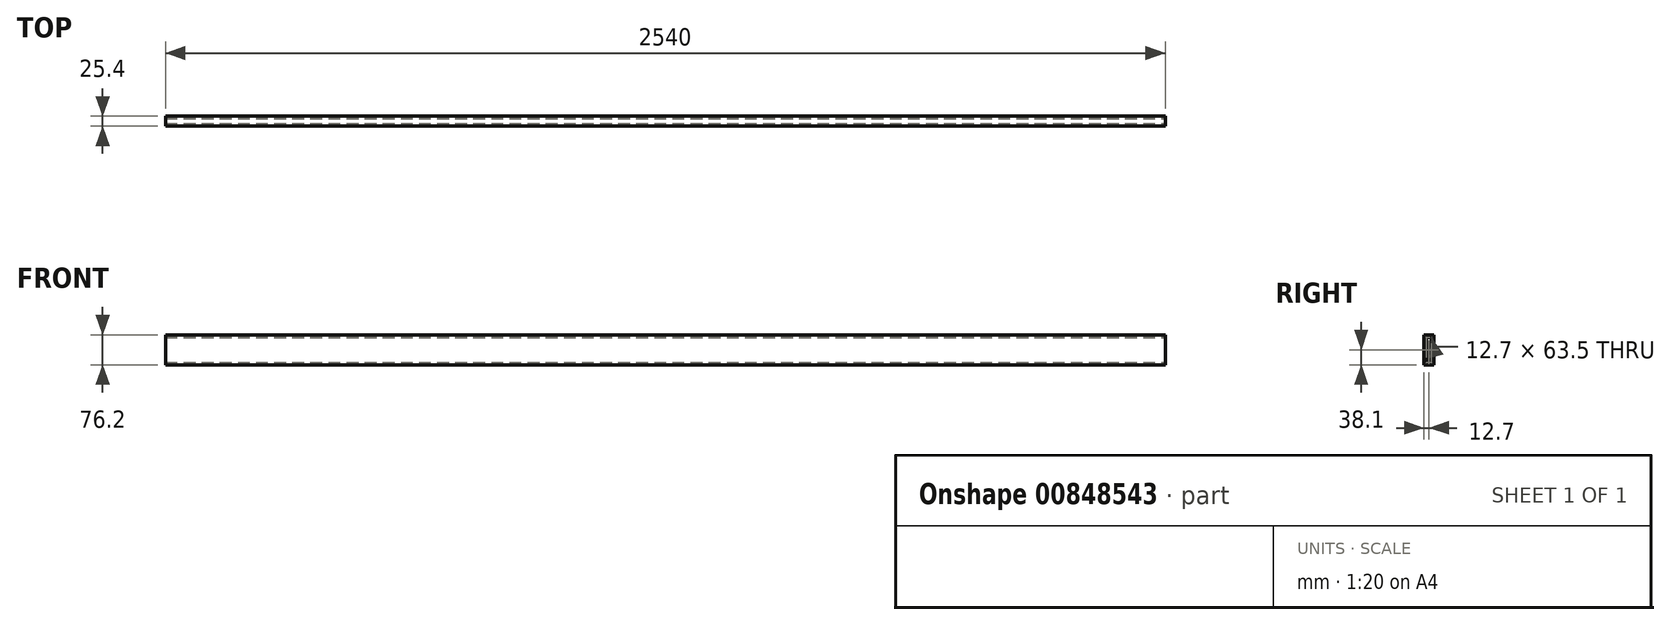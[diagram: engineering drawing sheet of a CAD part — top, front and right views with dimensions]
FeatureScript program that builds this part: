
annotation { "Feature Type Name" : "Feature", "Feature Type Description" : "" }
export const myFeature = defineFeature(function(context is Context, id is Id, definition is map)
    precondition{}
    {
        {
            var Q0;
            Q0=qCreatedBy(makeId("Top.planeOp"),FACE);
            var sketch = newSketch(context, id + "F0", { "sketchPlane" : qUnion([Q0])});
            skLineSegment(sketch, "E0.bottom", {"start": v(-1270, -12.7) * mm, "end": v(1270, -12.7) * mm});
            skLineSegment(sketch, "E0.top", {"start": v(-1270, 12.7) * mm, "end": v(1270, 12.7) * mm});
            skLineSegment(sketch, "E0.left", {"start": v(-1270, -12.7) * mm, "end": v(-1270, 12.7) * mm});
            skLineSegment(sketch, "E0.right", {"start": v(1270, -12.7) * mm, "end": v(1270, 12.7) * mm});
            skPoint(sketch, "E0.middle", {"position": v(0, 0) * mm});
            skSolve(sketch);
        }
        {
            var Q0;
            Q0 = qSketchRegion(id + "F0", true);
            extrude(context, id + "F1", {"entities" : qUnion([Q0]), "depth" : 76.2 * mm, "offsetDistance" : 25.4 * mm});
        }
        {
            var Q0;
            Q0=makeQuery(id+"F1.opExtrude","SWEPT_FACE",FACE,{"disambiguationData":[OSD([sQuery(id+"F0.wireOp",EDGE,"E0.right")])]});
            var Q1;
            Q1=makeQuery(id+"F1.opExtrude","SWEPT_FACE",FACE,{"disambiguationData":[OSD([sQuery(id+"F0.wireOp",EDGE,"E0.left")])]});
            var Q2;
            Q2=makeQuery(id+"F1.opExtrude","SWEPT_BODY",BODY,{"disambiguationData":[OSD([sQuery(id+"F0.wireOp",EDGE,"E0.bottom"),sQuery(id+"F0.wireOp",EDGE,"E0.top"),sQuery(id+"F0.wireOp",EDGE,"E0.left"),sQuery(id+"F0.wireOp",EDGE,"E0.right")])]});
            shell(context, id + "F2", {"entities" : qUnion([Q0, Q1]), "parts" : qUnion([Q2]), "thickness" : 6.35 * mm});
        }
    });
